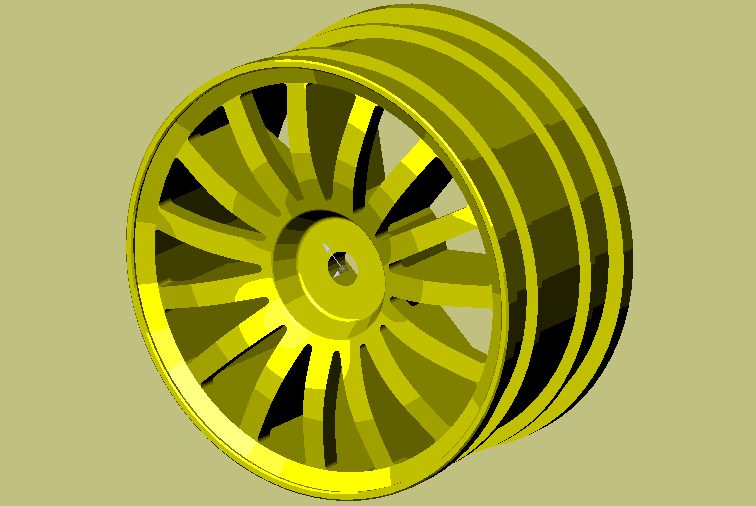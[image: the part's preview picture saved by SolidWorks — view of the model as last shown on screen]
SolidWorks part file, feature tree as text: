
SOLIDWORKS PART (.sldprt)
format: sldprt  version: not decoded by parser v0  size: 676,864 bytes
history: native  units: mm
features: sketch x7, plane x3, cut_extrude x3, extrude x2, revolve x2, pattern_circular x2, material x1, fillet x1, chamfer x1 (+8 scaffold rows collapsed)
feature tree (30):
  scaffold x8  (default folders/planes/origin — collapsed)
  material  "Matériau <non spécifié>"
  plane  "Plane1"
  plane  "Plane2"
  plane  "Plane3"
  sketch  "Esquisse1"  dims[D1=15.0mm]
  extrude  "Base-Extrusion"  Depth=10mm
  sketch  "Esquisse2"  dims[c1.D1=3.5mm c1.D2=7.5mm c2.D1=3.0mm c2.D2=1.5mm c2.D3=8.0mm c2.D4=2.0mm c2.D5=22.5mm c2.D6=1.0mm c2.D7=2.0mm c2.D8=22.5mm c2.D9=2.0mm c3.D7=2.5mm c3.D8=3.0mm c3.D10=2.5mm c3.D11=2.5mm c3.D12=~3.605551mm c3.D9=7.5mm c4.D12=~10.763932mm c4.D8=6.0mm c4.D9=7.5mm c4.D7=1.0mm c5.D9=2.5mm]
  revolve  "Boss.-Révol.1"  Angle=360deg
  sketch  "Esquisse3"  dims[D1=2.0mm D2=1.0mm D3=0.5mm D4=2.0mm D5=2.0mm D6=5.0mm D7=1.5mm D8=1.5mm D9=1.0mm D10=5.0mm]
  revolve  "Boss.-Révol.2"  Angle=360deg
  sketch  "Esquisse4"  dims[c1.D1=0.5mm c1.D3=22.5mm c1.D4=0.5mm c1.D2=~19.562579mm c2.D2=25.0deg c2.D3=4.0mm c2.D4=4.0mm c2.D5=~21.917413mm c3.D5=12.5deg]
  cut_extrude  "Enlèv. mat.-Extru.1"  Depth=10mm
  pattern_circular  "Répétition circulaire1"  Count=15 Angle=24deg
  fillet  "Congé1"  Radius=0.5mm
  chamfer  "Chanfrein2"  Distance=0.2mm Angle=45deg
  sketch  "Esquisse5"  dims[D1=12.0mm]
  cut_extrude  "Enlèv. mat.-Extru.2"  Depth=6.5mm
  sketch  "Esquisse6"  dims[D1=4.0mm]
  cut_extrude  "Enlèv. mat.-Extru.3"  [1 undecoded]
  sketch  "Esquisse9"
  extrude  "Boss.-Extru.2"  Depth=1mm
  pattern_circular  "Répétition circulaire2"  Count=8 Angle=48deg
decode coverage: 16 of 18 modeling features carry decoded parameters
note: ~ marks probable driven/reference dimensions
note: 1 parameter value undecoded
note: suppression state not decoded; provenance and decode notes live in map.json
